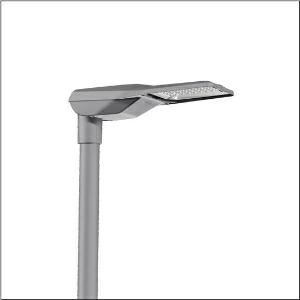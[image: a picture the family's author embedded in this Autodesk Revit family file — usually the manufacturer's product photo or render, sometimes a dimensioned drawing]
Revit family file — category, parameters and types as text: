
# Revit family: streetlight_sl_21_iq_mini___st0_8a_5xe2c31d08hb_f94e
name_source: partatom
category: Lighting Fixtures
units: mm (PartAtom-declared; Revit-internal decimal feet)

## family parameters
Cut with Voids When Loaded = No
Host = Face
Light Source = No
Part Type = Normal
Room Calculation Point = No
Round Connector Dimension = Use Diameter
Shared = No

## types (1)
- --- (1 x LED, 9450 lm, 70.9 W, 3000K)
    Apparent Load = 71 VA
    CIE Flux Codes = 38 75 97 100 100
    Color Rendering = 70
    Color Temperature = 3000K
    Default Elevation = 1800 mm
    Description = Streetlight SL 21 iQ mini, mast luminaire, primary light control with lens, of PMMA, primary optical cover: cover, of toughened safety glass, transparent, light distribution: ST0.8a, light emission: direct distribution, primary light characteristic: asymmetric, installation type: post-top, side-entry, LED, High Power LED, rated luminous flux: 9.450lm, luminous efficacy: 133lm/W, light colour: 730, colour temperature: 3000K, control: Auto-Match, Temp-Guard, Lumen-Switch, Night-Set, Smart-Wire, Light-Fading, Desk-Remote (wireless, voltage-free reading and setting of iQ features in the workshop via application-optimized NFC function/RFID function), optimised constant luminous flux control (CLO 2.0), pre-setting: linear dimming characteristic, mains connection: 220..240V, AC, 50/60Hz, start of lifetime: 71W, end of service life: 75W, reduction: 31W, luminaire housing, of diecast aluminium, powder-coated, Siteco® metallic grey (DB 702S), corrosivity category C5 mid according to DIN EN ISO 12944, please order mast flange separately, inclination adjustable: 0°, 5°, 10°, 15°, sealing non-destructively replaceable, multi-level sealing system, length: 628mm, width: 235mm, height: 110mm, mast flange for spigot size: 42mm (side-entry): 5XC10008XM4, 60/48mm (side-entry/post-top): 5XC10108XM2, 76/60mm (side-entry/post-top): 5XC10108XM1, protection rating (complete): IP66, insulation class (complete): insulation class II (safety insulation), certification: CE, ENEC, ENEC+, VDE, impact resistance: IK09, permissible operating ambient temperature for outdoor applications: -40..+50°C, standard-compliant lighting for roads and squares, packaging unit: 1 piece

Light Distribution: ST0.8a
    Height = 110 mm
    Lamp = 1 x LED
    Lamp Light Flux = 9450 lm
    Lamp Power = 70.9 W
    Lamp count = 1
    Length = 625 mm
    Luminous efficacy = 133 lm/W
    Manufacturer = Siteco
    ModVariant = No
    Model = 5XE2C31D08HB
    Number of Poles = 1
    OnlyDefault = Yes
    Power Factor = 1
    Product Name = Streetlight SL 21 iQ mini | ST0.8a
    Product group = mast luminaire | pylon top
    ProductGroupID = 6100
    Protection Class = Protection class II
    Protection Degree = IP 66
    RLX_Detail_Level = 1
    RLX_Emergency_Light_Flux = 0 lm
    RLX_Emergency_Type = 0
    RLX_Emergency_Type_DB = No
    RlxData = <blob elided: 91989 chars, md5=5b42caa3>
    Socket = socket
    Standby Power = 0 W
    System Light Flux = 9450 lm
    System Power = 71 W
    Type Comments = factory setting: luminous flux: 100 % | dim-lin: 254 | 711 mA
    Type Image = l_1003519.jpg
    URL = http://relux.com
    VarID = @adj_127799
    Voltage = 0 V
    Weight = 0.00 kg
    Width = 234 mm

## geometry (parser evidence)
native form markers: Blend x4, Sweep x10
no freeform markers — native parametric forms only
